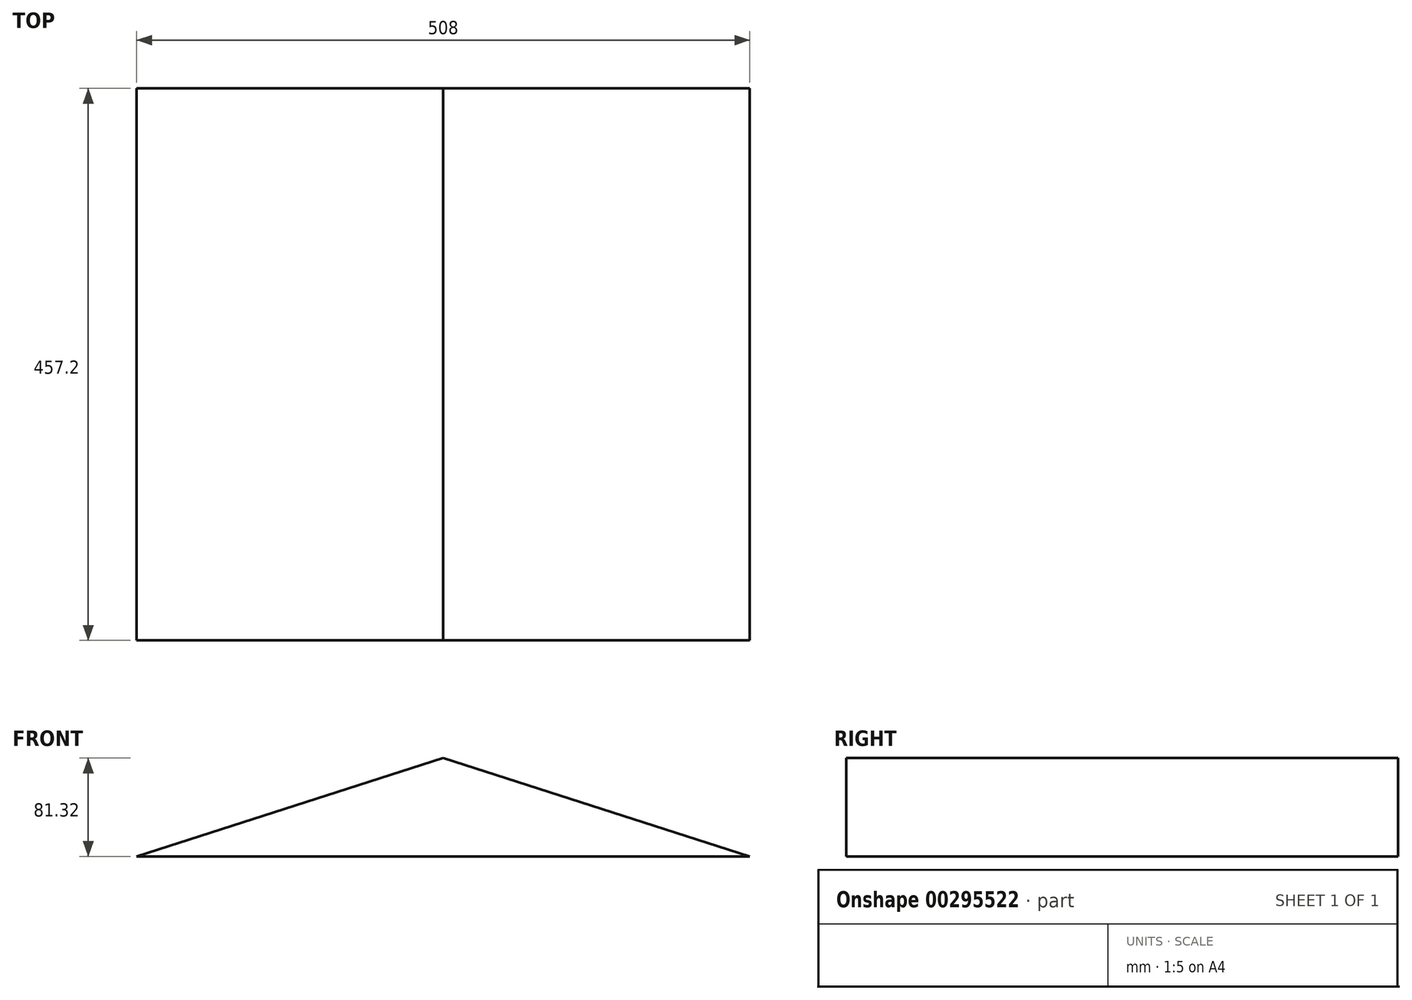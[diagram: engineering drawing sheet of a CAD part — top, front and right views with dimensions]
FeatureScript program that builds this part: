
annotation { "Feature Type Name" : "Feature", "Feature Type Description" : "" }
export const myFeature = defineFeature(function(context is Context, id is Id, definition is map)
    precondition{}
    {
        {
            var Q0;
            Q0=qCreatedBy(makeId("Front.planeOp"),FACE);
            var sketch = newSketch(context, id + "F0", { "sketchPlane" : qUnion([Q0])});
            skLineSegment(sketch, "E0", {"start": v(0, 0) * mm, "end": v(508, 0) * mm});
            skLineSegment(sketch, "E1", {"start": v(508, 0) * mm, "end": v(254, 81.32) * mm});
            skLineSegment(sketch, "E2", {"start": v(254, 81.32) * mm, "end": v(0, 0) * mm});
            skSolve(sketch);
        }
        {
            var Q0;
            Q0=makeQuery(id+"F0.imprint","IMPRINT",FACE,{"disambiguationData":[TD([[makeQuery(id+"F0.imprint","IMPRINT",EDGE,{"derivedFrom":sQuery(id+"F0.wireOp",EDGE,"E0")}),1.0]])]});
            extrude(context, id + "F1", {"entities" : qUnion([Q0]), "depth" : 457.2 * mm});
        }
    });
